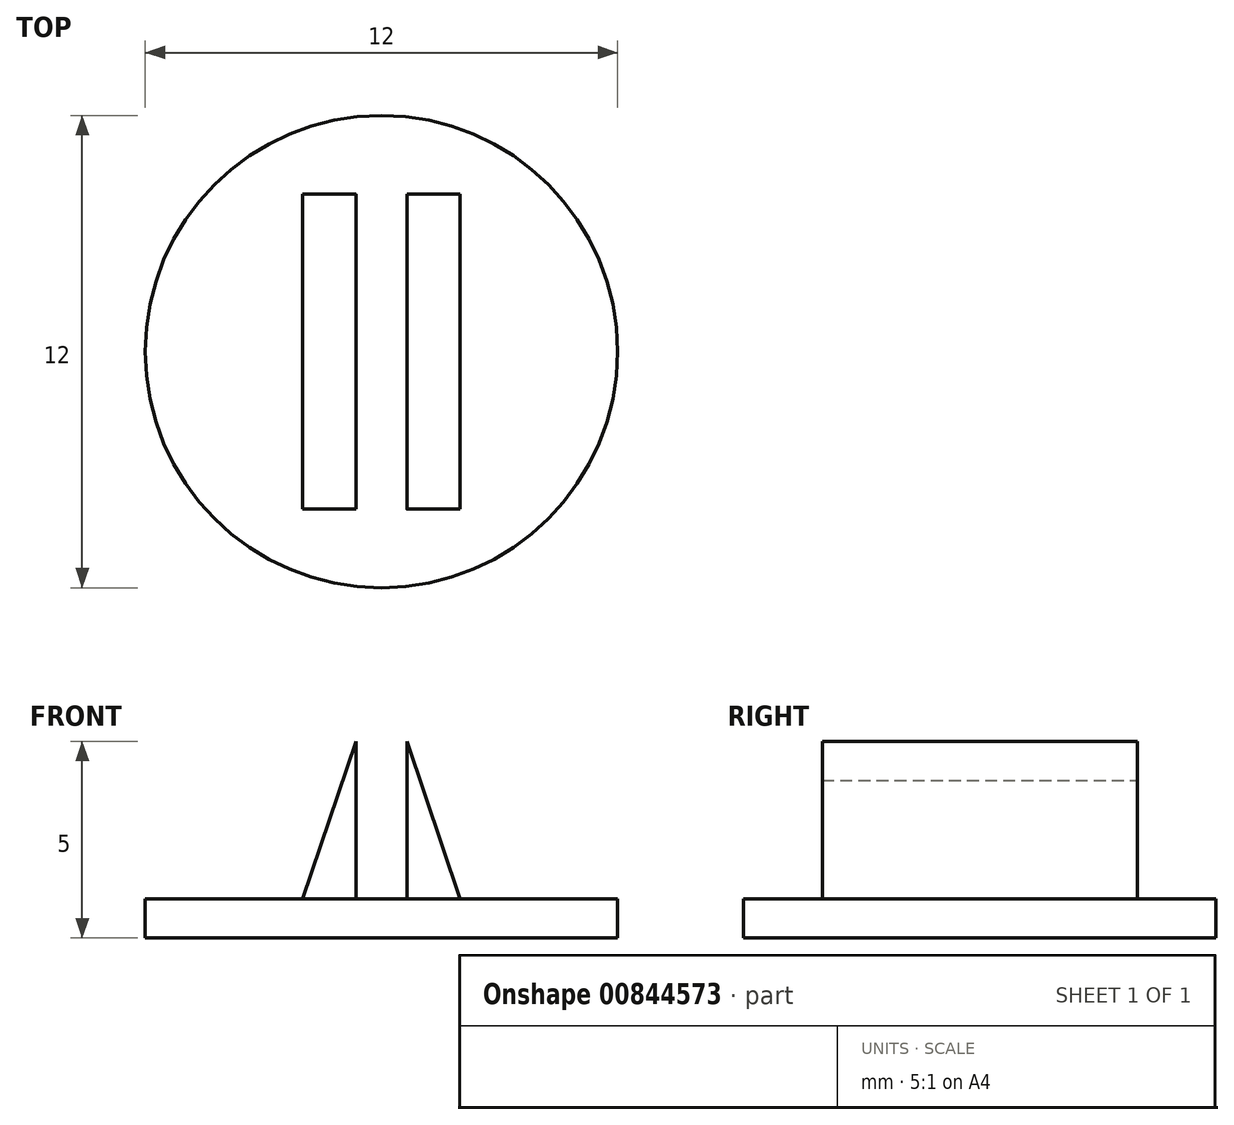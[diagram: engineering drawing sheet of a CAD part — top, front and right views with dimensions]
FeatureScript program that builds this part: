
annotation { "Feature Type Name" : "Feature", "Feature Type Description" : "" }
export const myFeature = defineFeature(function(context is Context, id is Id, definition is map)
    precondition{}
    {
        {
            var Q0;
            Q0=qCreatedBy(makeId("Top.planeOp"),FACE);
            var sketch = newSketch(context, id + "F0", { "sketchPlane" : qUnion([Q0])});
            skCircle(sketch, "E0", {"center": v(0, 0) * mm, "radius": 6 * mm});
            skSolve(sketch);
        }
        {
            var Q0;
            Q0=makeQuery(id+"F0.imprint","IMPRINT",FACE,{"disambiguationData":[TD([[makeQuery(id+"F0.imprint","IMPRINT",EDGE,{"derivedFrom":sQuery(id+"F0.wireOp",EDGE,"E0")}),1.0]])]});
            var Q1;
            Q1=sQuery(id+"F0.wireOp",EDGE,"E0");
            extrude(context, id + "F1", {"entities" : qUnion([Q0]), "surfaceEntities" : qUnion([Q1]), "depth" : 1 * mm, "offsetDistance" : 25 * mm});
        }
        {
            var Q0;
            Q0=qCreatedBy(makeId("Front.planeOp"),FACE);
            var sketch = newSketch(context, id + "F2", { "sketchPlane" : qUnion([Q0])});
            skLineSegment(sketch, "E1", {"start": v(-2, 1) * mm, "end": v(-0.65, 5) * mm});
            skLineSegment(sketch, "E2", {"start": v(-0.65, 5) * mm, "end": v(-0.65, 1) * mm});
            skLineSegment(sketch, "E3", {"start": v(-0.65, 1) * mm, "end": v(0.65, 1) * mm});
            skLineSegment(sketch, "E4", {"start": v(0.65, 1) * mm, "end": v(0.65, 5) * mm});
            skLineSegment(sketch, "E5", {"start": v(0.65, 5) * mm, "end": v(2, 1) * mm});
            skLineSegment(sketch, "E6", {"start": v(2, 1) * mm, "end": v(-2, 1) * mm});
            skArc(sketch, "E7", {"start": v(0.65, 5) * mm, "mid": v(0.64, 4.5) * mm, "end": v(0.65, 4) * mm});
            skArc(sketch, "E8", {"start": v(-0.65, 4) * mm, "mid": v(-0.64, 4.5) * mm, "end": v(-0.65, 5) * mm});
            skSolve(sketch);
        }
        {
            var Q0;
            Q0 = qSketchRegion(id + "F2", true);
            extrude(context, id + "F3", {"entities" : qUnion([Q0]), "operationType" : NewBodyOperationType.ADD, "endBound" : BoundingType.SYMMETRIC, "depth" : 8 * mm, "offsetDistance" : 25 * mm});
        }
    });
